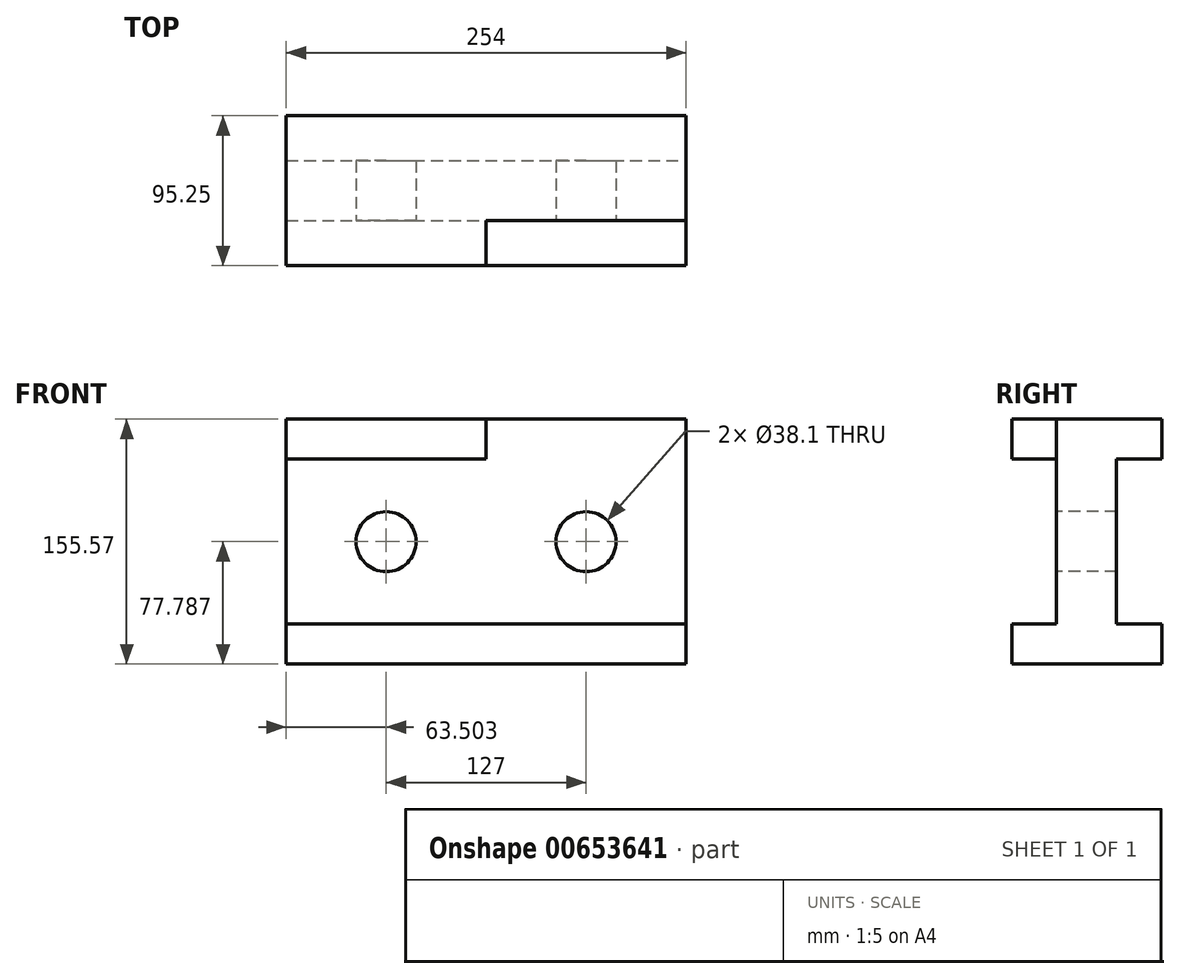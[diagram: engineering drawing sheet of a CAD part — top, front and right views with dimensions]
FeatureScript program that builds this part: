
annotation { "Feature Type Name" : "Feature", "Feature Type Description" : "" }
export const myFeature = defineFeature(function(context is Context, id is Id, definition is map)
    precondition{}
    {
        {
            var Q0;
            Q0=qCreatedBy(makeId("Front.planeOp"),FACE);
            var sketch = newSketch(context, id + "F0", { "sketchPlane" : qUnion([Q0])});
            skLineSegment(sketch, "E0.bottom", {"start": v(-135.4, 43.15) * mm, "end": v(118.6, 43.15) * mm});
            skLineSegment(sketch, "E0.top", {"start": v(-135.4, -112.42) * mm, "end": v(118.6, -112.42) * mm});
            skLineSegment(sketch, "E0.left", {"start": v(-135.4, 43.15) * mm, "end": v(-135.4, -112.42) * mm});
            skLineSegment(sketch, "E0.right", {"start": v(118.6, 43.15) * mm, "end": v(118.6, -112.42) * mm});
            skSolve(sketch);
        }
        {
            var Q0;
            Q0 = qSketchRegion(id + "F0", true);
            extrude(context, id + "F1", {"entities" : qUnion([Q0]), "depth" : 95.25 * mm, "offsetDistance" : 25.4 * mm});
        }
        {
            var Q0;
            Q0=makeQuery(id+"F1.opExtrude","CAP_FACE",FACE,{"disambiguationData":[OSD([sQuery(id+"F0.wireOp",EDGE,"E0.bottom"),sQuery(id+"F0.wireOp",EDGE,"E0.top"),sQuery(id+"F0.wireOp",EDGE,"E0.left"),sQuery(id+"F0.wireOp",EDGE,"E0.right")])],"isStart":false});
            var sketch = newSketch(context, id + "F2", { "sketchPlane" : qUnion([Q0])});
            skLineSegment(sketch, "E1.bottom", {"start": v(-135.4, 17.75) * mm, "end": v(118.6, 17.75) * mm});
            skLineSegment(sketch, "E1.top", {"start": v(-135.4, -87.02) * mm, "end": v(118.6, -87.02) * mm});
            skLineSegment(sketch, "E1.left", {"start": v(-135.4, 17.75) * mm, "end": v(-135.4, -87.02) * mm});
            skLineSegment(sketch, "E1.right", {"start": v(118.6, 17.75) * mm, "end": v(118.6, -87.02) * mm});
            skSolve(sketch);
        }
        {
            var Q0;
            Q0=makeQuery(id+"F2.imprint","IMPRINT",FACE,{"disambiguationData":[TD([[makeQuery(id+"F2.imprint","IMPRINT",EDGE,{"derivedFrom":sQuery(id+"F2.wireOp",EDGE,"E1.bottom")}),-1.0]])]});
            extrude(context, id + "F3", {"entities" : qUnion([Q0]), "operationType" : NewBodyOperationType.REMOVE, "oppositeDirection" : true, "depth" : 28.57 * mm, "offsetDistance" : 25.4 * mm});
        }
        {
            var Q0;
            {var subQ0=sQuery(id+"F0.wireOp",EDGE,"E0.bottom");var subQ1=sQuery(id+"F0.wireOp",EDGE,"E0.right");var subQ2=sQuery(id+"F0.wireOp",EDGE,"E0.left");Q0=makeQuery(id+"F3.boolean.opBoolean","SPLIT",FACE,{"disambiguationData":[TD([makeQuery(id+"F1.opExtrude","SWEPT_FACE",FACE,{"disambiguationData":[OSD([subQ0])]})])],"derivedFrom":makeQuery(id+"F1.opExtrude","CAP_FACE",FACE,{"disambiguationData":[OSD([subQ0,sQuery(id+"F0.wireOp",EDGE,"E0.top"),subQ2,subQ1])],"isStart":false})});}
            var sketch = newSketch(context, id + "F4", { "sketchPlane" : qUnion([Q0])});
            skLineSegment(sketch, "E2.bottom", {"start": v(118.6, 17.75) * mm, "end": v(-8.4, 17.75) * mm});
            skLineSegment(sketch, "E2.top", {"start": v(118.6, 43.15) * mm, "end": v(-8.4, 43.15) * mm});
            skLineSegment(sketch, "E2.left", {"start": v(118.6, 17.75) * mm, "end": v(118.6, 43.15) * mm});
            skLineSegment(sketch, "E2.right", {"start": v(-8.4, 17.75) * mm, "end": v(-8.4, 43.15) * mm});
            skSolve(sketch);
        }
        {
            var Q0;
            Q0 = qSketchRegion(id + "F4", true);
            extrude(context, id + "F5", {"entities" : qUnion([Q0]), "operationType" : NewBodyOperationType.REMOVE, "oppositeDirection" : true, "depth" : 28.57 * mm, "offsetDistance" : 25.4 * mm});
        }
        {
            var Q0;
            Q0=makeQuery(id+"F5.boolean.opBoolean","MERGE",FACE,{"derivedFrom":[makeQuery(id+"F3.boolean.opBoolean","COPY",FACE,{"derivedFrom":makeQuery(id+"F3.opExtrude","CAP_FACE",FACE,{"disambiguationData":[OSD([sQuery(id+"F2.wireOp",EDGE,"E1.bottom"),sQuery(id+"F2.wireOp",EDGE,"E1.top"),sQuery(id+"F2.wireOp",EDGE,"E1.left"),sQuery(id+"F2.wireOp",EDGE,"E1.right")])],"isStart":false})}),makeQuery(id+"F5.opExtrude","CAP_FACE",FACE,{"disambiguationData":[OSD([sQuery(id+"F4.wireOp",EDGE,"E2.bottom"),sQuery(id+"F4.wireOp",EDGE,"E2.top"),sQuery(id+"F4.wireOp",EDGE,"E2.left"),sQuery(id+"F4.wireOp",EDGE,"E2.right")])],"isStart":false})]});
            var sketch = newSketch(context, id + "F6", { "sketchPlane" : qUnion([Q0])});
            skCircle(sketch, "E3", {"center": v(-71.9, -34.63) * mm, "radius": 19.05 * mm});
            skCircle(sketch, "E4", {"center": v(55.1, -34.63) * mm, "radius": 19.05 * mm});
            skSolve(sketch);
        }
        {
            var Q0;
            Q0=makeQuery(id+"F6.imprint","IMPRINT",FACE,{"disambiguationData":[TD([[makeQuery(id+"F6.imprint","IMPRINT",EDGE,{"derivedFrom":sQuery(id+"F6.wireOp",EDGE,"E4")}),1.0]])]});
            var Q1;
            Q1=makeQuery(id+"F6.imprint","IMPRINT",FACE,{"disambiguationData":[TD([[makeQuery(id+"F6.imprint","IMPRINT",EDGE,{"derivedFrom":sQuery(id+"F6.wireOp",EDGE,"E3")}),1.0]])]});
            extrude(context, id + "F7", {"entities" : qUnion([Q0, Q1]), "operationType" : NewBodyOperationType.REMOVE, "endBound" : BoundingType.THROUGH_ALL, "oppositeDirection" : true, "depth" : 25.4 * mm, "offsetDistance" : 25.4 * mm});
        }
        {
            var Q0;
            Q0=makeQuery(id+"F1.opExtrude","SWEPT_FACE",FACE,{"disambiguationData":[OSD([sQuery(id+"F0.wireOp",EDGE,"E0.right")])]});
            var sketch = newSketch(context, id + "F8", { "sketchPlane" : qUnion([Q0])});
            skLineSegment(sketch, "E5.bottom", {"start": v(0, -87.02) * mm, "end": v(-28.57, -87.02) * mm});
            skLineSegment(sketch, "E5.top", {"start": v(0, 17.75) * mm, "end": v(-28.58, 17.75) * mm});
            skLineSegment(sketch, "E5.left", {"start": v(0, -87.02) * mm, "end": v(0, 17.75) * mm});
            skLineSegment(sketch, "E5.right", {"start": v(-28.57, -87.02) * mm, "end": v(-28.58, 17.75) * mm});
            skSolve(sketch);
        }
        {
            var Q0;
            Q0=makeQuery(id+"F8.imprint","IMPRINT",FACE,{"disambiguationData":[TD([[makeQuery(id+"F8.imprint","IMPRINT",EDGE,{"derivedFrom":sQuery(id+"F8.wireOp",EDGE,"E5.bottom")}),-1.0]])]});
            extrude(context, id + "F9", {"entities" : qUnion([Q0]), "operationType" : NewBodyOperationType.REMOVE, "endBound" : BoundingType.THROUGH_ALL, "oppositeDirection" : true, "depth" : 25.4 * mm, "offsetDistance" : 25.4 * mm});
        }
    });
